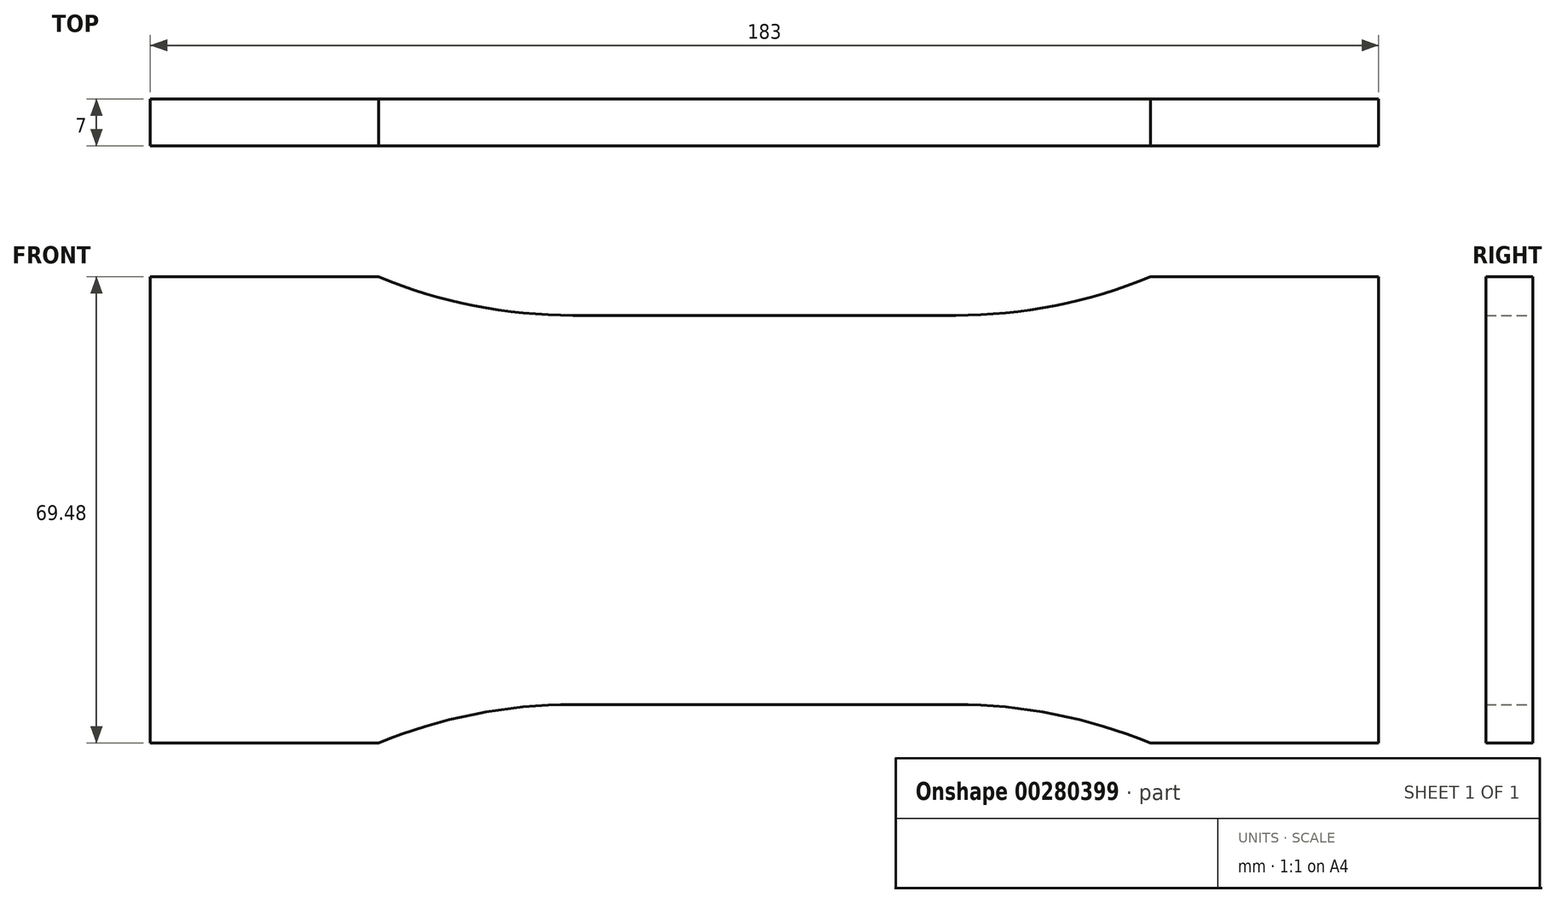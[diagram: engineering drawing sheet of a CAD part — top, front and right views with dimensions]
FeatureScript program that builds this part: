
annotation { "Feature Type Name" : "Feature", "Feature Type Description" : "" }
export const myFeature = defineFeature(function(context is Context, id is Id, definition is map)
    precondition{}
    {
        {
            var Q0;
            Q0=qCreatedBy(makeId("Front.planeOp"),FACE);
            var sketch = newSketch(context, id + "F0", { "sketchPlane" : qUnion([Q0])});
            skLineSegment(sketch, "E0", {"start": v(0, 28.99) * mm, "end": v(28.5, 28.99) * mm});
            skArc(sketch, "E1", {"start": v(28.5, 28.99) * mm, "mid": v(43.28, 30.44) * mm, "end": v(57.5, 34.74) * mm});
            skLineSegment(sketch, "E2", {"start": v(91.5, 34.74) * mm, "end": v(91.5, 0) * mm});
            skLineSegment(sketch, "E3", {"start": v(91.5, 34.74) * mm, "end": v(57.5, 34.74) * mm});
            skLineSegment(sketch, "E4.MirrorCS", {"start": v(91.5, -34.74) * mm, "end": v(91.5, 0) * mm});
            skLineSegment(sketch, "E5.MirrorCS", {"start": v(91.5, -34.74) * mm, "end": v(57.5, -34.74) * mm});
            skArc(sketch, "E6.MirrorCS", {"start": v(28.5, -28.99) * mm, "mid": v(43.28, -30.44) * mm, "end": v(57.5, -34.74) * mm});
            skLineSegment(sketch, "E7.MirrorCS", {"start": v(0, -28.99) * mm, "end": v(28.5, -28.99) * mm});
            skLineSegment(sketch, "E8.MirrorCS", {"start": v(0, 28.99) * mm, "end": v(-28.5, 28.99) * mm});
            skArc(sketch, "E9.MirrorCS", {"start": v(-28.5, 28.99) * mm, "mid": v(-43.28, 30.44) * mm, "end": v(-57.5, 34.74) * mm});
            skLineSegment(sketch, "E10.MirrorCS", {"start": v(-91.5, 34.74) * mm, "end": v(-57.5, 34.74) * mm});
            skLineSegment(sketch, "E11.MirrorCS", {"start": v(-91.5, 34.74) * mm, "end": v(-91.5, 0) * mm});
            skLineSegment(sketch, "E12.MirrorCS", {"start": v(-91.5, -34.74) * mm, "end": v(-91.5, 0) * mm});
            skLineSegment(sketch, "E13.MirrorCS", {"start": v(-91.5, -34.74) * mm, "end": v(-57.5, -34.74) * mm});
            skArc(sketch, "E14.MirrorCS", {"start": v(-28.5, -28.99) * mm, "mid": v(-43.28, -30.44) * mm, "end": v(-57.5, -34.74) * mm});
            skLineSegment(sketch, "E15.MirrorCS", {"start": v(0, -28.99) * mm, "end": v(-28.5, -28.99) * mm});
            skSolve(sketch);
        }
        {
            var Q0;
            Q0 = qSketchRegion(id + "F0", true);
            extrude(context, id + "F1", {"entities" : qUnion([Q0]), "endBound" : BoundingType.SYMMETRIC, "depth" : 7 * mm});
        }
    });
